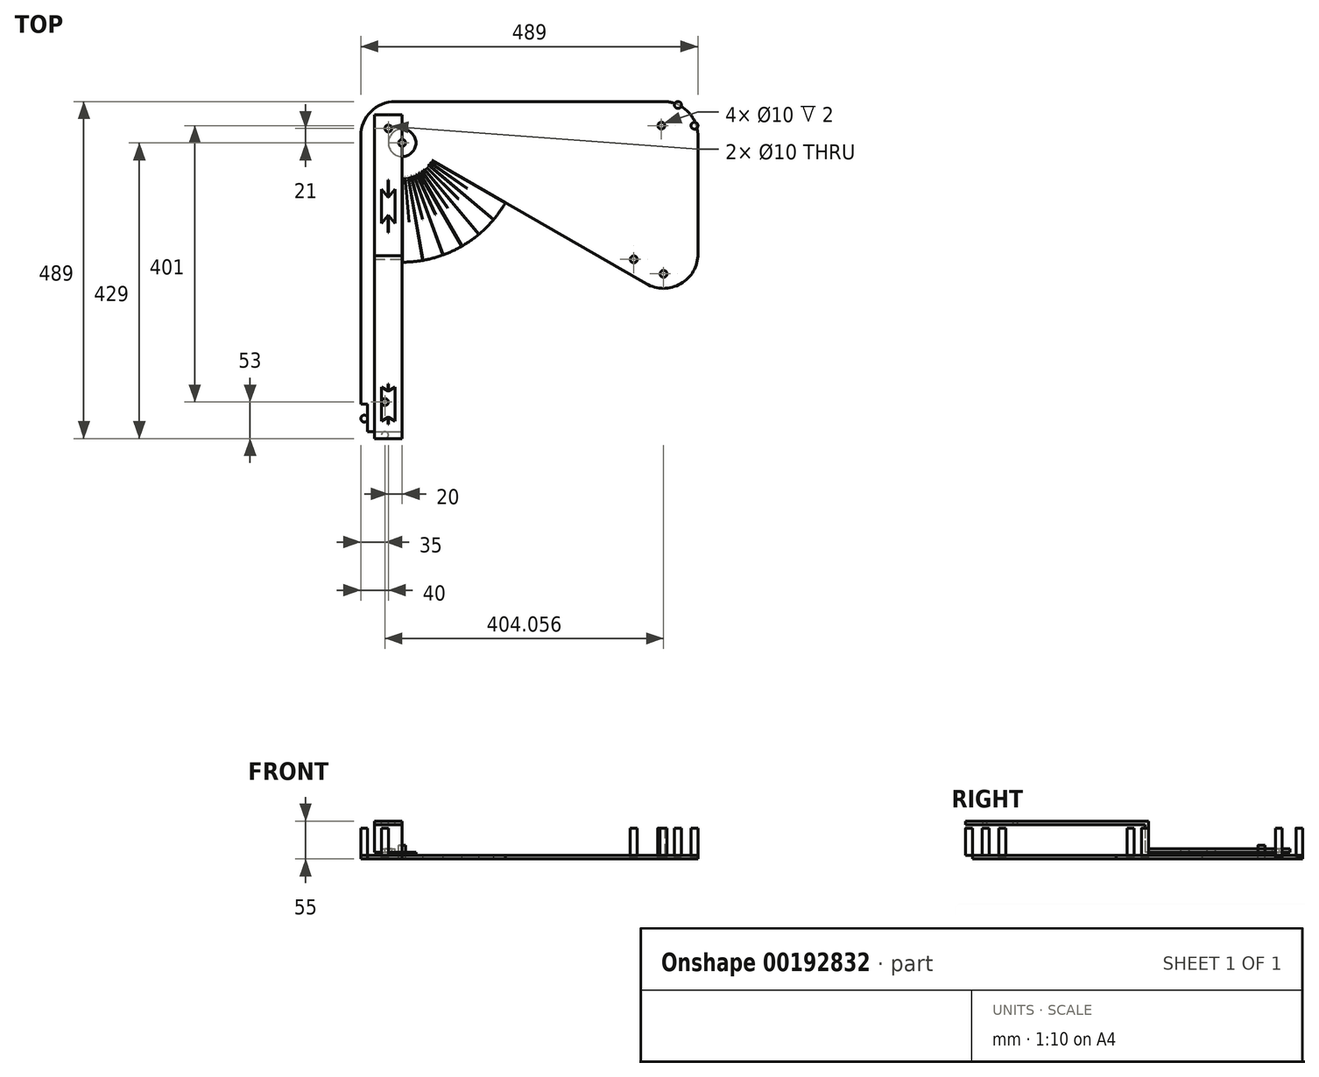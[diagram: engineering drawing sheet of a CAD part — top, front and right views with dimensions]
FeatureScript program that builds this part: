
annotation { "Feature Type Name" : "Feature", "Feature Type Description" : "" }
export const myFeature = defineFeature(function(context is Context, id is Id, definition is map)
    precondition{}
    {
        {
            var Q0;
            Q0=qCreatedBy(makeId("Top.planeOp"),FACE);
            var sketch = newSketch(context, id + "F0", { "sketchPlane" : qUnion([Q0])});
            skLineSegment(sketch, "E0.bottom", {"start": v(0, 0) * mm, "end": v(489, 0) * mm});
            skLineSegment(sketch, "E0.left", {"start": v(0, 0) * mm, "end": v(0, 500) * mm});
            skLineSegment(sketch, "E0.right", {"start": v(489, 0) * mm, "end": v(489, 479) * mm});
            skLineSegment(sketch, "E1.top", {"start": v(0, 0) * mm, "end": v(10, 0) * mm});
            skLineSegment(sketch, "E1.left", {"start": v(0, 489) * mm, "end": v(0, 0) * mm});
            skLineSegment(sketch, "E1.right", {"start": v(10, 50) * mm, "end": v(10, 10) * mm});
            skPoint(sketch, "E2", {"position": v(60, 429) * mm});
            skLineSegment(sketch, "E3", {"start": v(60, 255.9) * mm, "end": v(60, 0) * mm});
            skLineSegment(sketch, "E4", {"start": v(209.9, 342.45) * mm, "end": v(489, 181.32) * mm});
            skLineSegment(sketch, "E5.bottom", {"start": v(10, 48) * mm, "end": v(60, 48) * mm, "construction": true});
            skLineSegment(sketch, "E5.right", {"start": v(60, 48) * mm, "end": v(60, 10) * mm, "construction": true});
            skLineSegment(sketch, "E6.top", {"start": v(441, 429) * mm, "end": v(479, 429) * mm, "construction": true});
            skLineSegment(sketch, "E6.left", {"start": v(441, 479) * mm, "end": v(441, 429) * mm, "construction": true});
            skArc(sketch, "E7", {"start": v(60, 29) * mm, "mid": v(342.84, 146.16) * mm, "end": v(460, 429) * mm, "construction": true});
            skPoint(sketch, "E8", {"position": v(10, 29) * mm});
            skPoint(sketch, "E9", {"position": v(460, 479) * mm});
            skArc(sketch, "E10.0", {"start": v(60, 10) * mm, "mid": v(356.28, 132.72) * mm, "end": v(479, 429) * mm, "construction": true});
            skArc(sketch, "E11.0", {"start": v(60, 48) * mm, "mid": v(329.4, 159.6) * mm, "end": v(441, 429) * mm, "construction": true});
            skLineSegment(sketch, "E12", {"start": v(60, 255.9) * mm, "end": v(209.9, 342.45) * mm, "construction": true});
            skPoint(sketch, "E13.end.orphan", {"position": v(189.9, 354) * mm});
            skPoint(sketch, "E13.start.orphan", {"position": v(60, 279) * mm});
            skCircle(sketch, "E14", {"center": v(60, 429) * mm, "radius": 5 * mm});
            skLineSegment(sketch, "E15.top", {"start": v(489, 489) * mm, "end": v(0, 489) * mm});
            skLineSegment(sketch, "E15.left", {"start": v(489, 479) * mm, "end": v(489, 489) * mm});
            skLineSegment(sketch, "E16", {"start": v(439, 489) * mm, "end": v(439, 479) * mm});
            skLineSegment(sketch, "E17", {"start": v(439, 479) * mm, "end": v(479, 479) * mm});
            skLineSegment(sketch, "E18", {"start": v(479, 479) * mm, "end": v(479, 429) * mm});
            skLineSegment(sketch, "E19", {"start": v(489, 429) * mm, "end": v(479, 429) * mm});
            skArc(sketch, "E20", {"start": v(60, 255.9) * mm, "mid": v(146.55, 279.1) * mm, "end": v(209.9, 342.45) * mm});
            skLineSegment(sketch, "E21", {"start": v(0, 50) * mm, "end": v(10, 50) * mm});
            skLineSegment(sketch, "E22", {"start": v(10, 10) * mm, "end": v(60, 10) * mm});
            skSolve(sketch);
        }
        {
            var Q0;
            {var subQ3=sQuery(id+"F0.wireOp",EDGE,"E1.right");Q0=makeQuery(id+"F0.imprint","IMPRINT",FACE,{"disambiguationData":[TD([[makeQuery(id+"F0.imprint","IMPRINT",EDGE,{"derivedFrom":subQ3}),1.0]])]});}
            var Q1;
            {var subQ2=sQuery(id+"F0.wireOp",EDGE,"E1.top");Q1=makeQuery(id+"F0.imprint","IMPRINT",FACE,{"disambiguationData":[TD([[makeQuery(id+"F0.imprint","IMPRINT",EDGE,{"derivedFrom":subQ2}),1.0]])]});}
            var Q2;
            {var subQ1=sQuery(id+"F0.wireOp",EDGE,"E15.left");Q2=makeQuery(id+"F0.imprint","IMPRINT",FACE,{"disambiguationData":[TD([[makeQuery(id+"F0.imprint","IMPRINT",EDGE,{"derivedFrom":subQ1}),1.0]])]});}
            extrude(context, id + "F1", {"entities" : qUnion([Q0, Q1, Q2]), "depth" : 5 * mm});
        }
        {
            var Q0;
            {var subQ0=sQuery(id+"F0.wireOp",EDGE,"E15.top");Q0=makeQuery(id+"FC8zW7vc6qnoxrJ_1.boolean.opBoolean","MERGE",FACE,{"derivedFrom":[makeQuery(id+"F1.opExtrude","SWEPT_FACE",FACE,{"disambiguationData":[OSD([subQ0])]}),makeQuery(id+"FC8zW7vc6qnoxrJ_1.opExtrude","SWEPT_FACE",FACE,{"disambiguationData":[OSD([subQ0]),TDD([makeQuery(id+"F0.imprint","IMPRINT",EDGE,{"disambiguationData":[TD([[makeQuery(id+"F0.imprint","INTERSECT",VERTEX,{"derivedFrom":[subQ0,sQuery(id+"F0.wireOp",EDGE,"E15.left")]}),-1.0]])],"derivedFrom":subQ0})])]}),makeQuery(id+"FC8zW7vc6qnoxrJ_1.opExtrude","SWEPT_FACE",FACE,{"disambiguationData":[OSD([subQ0]),TDD([makeQuery(id+"F0.imprint","IMPRINT",EDGE,{"disambiguationData":[TD([[makeQuery(id+"F0.imprint","INTERSECT",VERTEX,{"derivedFrom":[sQuery(id+"F0.wireOp",EDGE,"E1.left"),subQ0]}),1.0]])],"derivedFrom":subQ0})])]})]});}
            cPlane(context, id + "F2", {"entities" : qUnion([Q0]), "cplaneType" : CPlaneType.OFFSET, "offset" : 60 * mm, "oppositeDirection" : true, "width" : 150 * mm, "height" : 150 * mm});
        }
        {
            var Q0;
            Q0=qCreatedBy(id+"F2.planeOp",FACE);
            var sketch = newSketch(context, id + "F3", { "sketchPlane" : qUnion([Q0])});
            skLineSegment(sketch, "E23", {"start": v(-60, 20) * mm, "end": v(-60, 0) * mm});
            skLineSegment(sketch, "E24", {"start": v(-60, 20) * mm, "end": v(-65, 20) * mm});
            skLineSegment(sketch, "E25", {"start": v(-65, 20) * mm, "end": v(-65, 10) * mm});
            skLineSegment(sketch, "E26", {"start": v(-65, 10) * mm, "end": v(-80, 10) * mm});
            skLineSegment(sketch, "E27", {"start": v(-80, 10) * mm, "end": v(-80, 5) * mm});
            skLineSegment(sketch, "E28", {"start": v(-80, 5) * mm, "end": v(-65, 5) * mm});
            skLineSegment(sketch, "E29", {"start": v(-65, 5) * mm, "end": v(-65, 0) * mm});
            skLineSegment(sketch, "E30", {"start": v(-65, 0) * mm, "end": v(-60, 0) * mm});
            skSolve(sketch);
        }
        {
            var Q0;
            Q0=qSketchRegion(id+"F3",true);
            var Q1;
            Q1=sQuery(id+"F3.wireOp",EDGE,"E23");
            revolve(context, id + "F4", {"entities" : qUnion([Q0]), "axis" : qUnion([Q1]), "revolveType" : RevolveType.FULL});
        }
        {
            var Q0;
            Q0=makeQuery(id+"F1.opExtrude","CAP_FACE",FACE,{"disambiguationData":[OSD([sQuery(id+"F0.wireOp",EDGE,"E0.bottom"),sQuery(id+"F0.wireOp",EDGE,"E0.top"),sQuery(id+"F0.wireOp",EDGE,"E0.right"),sQuery(id+"F0.wireOp",EDGE,"E1.right"),sQuery(id+"F0.wireOp",EDGE,"E3"),sQuery(id+"F0.wireOp",EDGE,"E4"),sQuery(id+"F0.wireOp",EDGE,"E12"),sQuery(id+"F0.wireOp",EDGE,"E14")])],"isStart":false});
            cPlane(context, id + "F5", {"entities" : qUnion([Q0]), "cplaneType" : CPlaneType.OFFSET, "offset" : 0 * mm, "width" : 150 * mm, "height" : 150 * mm});
        }
        {
            var Q0;
            Q0=qCreatedBy(id+"F5.planeOp",FACE);
            var sketch = newSketch(context, id + "F6", { "sketchPlane" : qUnion([Q0])});
            skCircle(sketch, "E31", {"center": v(35, 53) * mm, "radius": 5 * mm});
            skLineSegment(sketch, "E32.bottom", {"start": v(10, 10) * mm, "end": v(60, 10) * mm, "construction": true});
            skLineSegment(sketch, "E32.top", {"start": v(10, 48) * mm, "end": v(60, 48) * mm, "construction": true});
            skLineSegment(sketch, "E32.left", {"start": v(10, 10) * mm, "end": v(10, 48) * mm, "construction": true});
            skLineSegment(sketch, "E32.right", {"start": v(60, 10) * mm, "end": v(60, 48) * mm, "construction": true});
            skLineSegment(sketch, "E33.bottom", {"start": v(479, 479) * mm, "end": v(441, 479) * mm, "construction": true});
            skLineSegment(sketch, "E33.top", {"start": v(479, 429) * mm, "end": v(441, 429) * mm, "construction": true});
            skLineSegment(sketch, "E33.left", {"start": v(479, 479) * mm, "end": v(479, 429) * mm, "construction": true});
            skLineSegment(sketch, "E33.right", {"start": v(441, 479) * mm, "end": v(441, 429) * mm, "construction": true});
            skArc(sketch, "E34", {"start": v(60, 29) * mm, "mid": v(342.84, 146.16) * mm, "end": v(460, 429) * mm, "construction": true});
            skArc(sketch, "E35.0", {"start": v(60, 10) * mm, "mid": v(356.28, 132.72) * mm, "end": v(479, 429) * mm, "construction": true});
            skArc(sketch, "E36.0", {"start": v(60, 48) * mm, "mid": v(329.4, 159.6) * mm, "end": v(441, 429) * mm, "construction": true});
            skLineSegment(sketch, "E37", {"start": v(460, 429) * mm, "end": v(460, 479) * mm, "construction": true});
            skLineSegment(sketch, "E38", {"start": v(60, 29) * mm, "end": v(10, 29) * mm, "construction": true});
            skCircle(sketch, "E39", {"center": v(436, 454) * mm, "radius": 5 * mm});
            skCircle(sketch, "E40", {"center": v(439.06, 239.02) * mm, "radius": 5 * mm});
            skLineSegment(sketch, "E41", {"start": v(439.06, 239.02) * mm, "end": v(395.9, 260.06) * mm, "construction": true});
            skCircle(sketch, "E42", {"center": v(395.9, 260.06) * mm, "radius": 5 * mm});
            skCircle(sketch, "E43.MirrorC", {"center": v(35, 5) * mm, "radius": 5 * mm});
            skCircle(sketch, "E44", {"center": v(5, 29) * mm, "radius": 5 * mm});
            skLineSegment(sketch, "E45", {"start": v(35, 5) * mm, "end": v(35, 53) * mm, "construction": true});
            skCircle(sketch, "E46.MirrorC", {"center": v(484, 454) * mm, "radius": 5 * mm});
            skLineSegment(sketch, "E47", {"start": v(436, 454) * mm, "end": v(484, 454) * mm, "construction": true});
            skCircle(sketch, "E48", {"center": v(460, 484) * mm, "radius": 5 * mm});
            skLineSegment(sketch, "E49", {"start": v(5, 34) * mm, "end": v(0, 34) * mm});
            skLineSegment(sketch, "E50", {"start": v(0, 34) * mm, "end": v(0, 24) * mm});
            skLineSegment(sketch, "E51", {"start": v(0, 24) * mm, "end": v(5, 24) * mm});
            skLineSegment(sketch, "E52.bottom", {"start": v(30, 5) * mm, "end": v(40, 5) * mm});
            skLineSegment(sketch, "E52.top", {"start": v(30, 0) * mm, "end": v(40, 0) * mm});
            skLineSegment(sketch, "E52.left", {"start": v(30, 5) * mm, "end": v(30, 0) * mm});
            skLineSegment(sketch, "E52.right", {"start": v(40, 5) * mm, "end": v(40, 0) * mm});
            skLineSegment(sketch, "E53.bottom", {"start": v(465, 484) * mm, "end": v(455, 484) * mm});
            skLineSegment(sketch, "E53.top", {"start": v(465, 489) * mm, "end": v(455, 489) * mm});
            skLineSegment(sketch, "E53.left", {"start": v(465, 484) * mm, "end": v(465, 489) * mm});
            skLineSegment(sketch, "E53.right", {"start": v(455, 484) * mm, "end": v(455, 489) * mm});
            skLineSegment(sketch, "E54.bottom", {"start": v(484, 459) * mm, "end": v(489, 459) * mm});
            skLineSegment(sketch, "E54.top", {"start": v(484, 449) * mm, "end": v(489, 449) * mm});
            skLineSegment(sketch, "E54.left", {"start": v(484, 459) * mm, "end": v(484, 449) * mm});
            skLineSegment(sketch, "E54.right", {"start": v(489, 459) * mm, "end": v(489, 449) * mm});
            skSolve(sketch);
        }
        {
            var Q0;
            Q0=makeQuery(id+"F6.imprint","IMPRINT",FACE,{"disambiguationData":[TD([[makeQuery(id+"F6.imprint","IMPRINT",EDGE,{"derivedFrom":sQuery(id+"F6.wireOp",EDGE,"E42")}),1.0]])]});
            var Q1;
            Q1=makeQuery(id+"F6.imprint","IMPRINT",FACE,{"disambiguationData":[TD([[makeQuery(id+"F6.imprint","IMPRINT",EDGE,{"derivedFrom":sQuery(id+"F6.wireOp",EDGE,"E40")}),1.0]])]});
            var Q2;
            Q2=makeQuery(id+"F6.imprint","IMPRINT",FACE,{"disambiguationData":[TD([[makeQuery(id+"F6.imprint","IMPRINT",EDGE,{"derivedFrom":sQuery(id+"F6.wireOp",EDGE,"E39")}),1.0]])]});
            var Q3;
            Q3=makeQuery(id+"F6.imprint","IMPRINT",FACE,{"disambiguationData":[TD([[makeQuery(id+"F6.imprint","IMPRINT",EDGE,{"derivedFrom":sQuery(id+"F6.wireOp",EDGE,"E31")}),1.0]])]});
            var Q4;
            {var subQ0=sQuery(id+"F6.wireOp",EDGE,"E54.left");Q4=makeQuery(id+"F6.imprint","IMPRINT",FACE,{"disambiguationData":[TD([[makeQuery(id+"F6.imprint","IMPRINT",EDGE,{"derivedFrom":subQ0}),-1.0]])]});}
            var Q5;
            {var subQ0=sQuery(id+"F6.wireOp",EDGE,"E54.left");Q5=makeQuery(id+"F6.imprint","IMPRINT",FACE,{"disambiguationData":[TD([[makeQuery(id+"F6.imprint","IMPRINT",EDGE,{"derivedFrom":subQ0}),1.0]])]});}
            var Q6;
            {var subQ0=sQuery(id+"F6.wireOp",EDGE,"E54.bottom");Q6=makeQuery(id+"F6.imprint","IMPRINT",FACE,{"disambiguationData":[TD([[makeQuery(id+"F6.imprint","IMPRINT",EDGE,{"derivedFrom":subQ0}),-1.0]])]});}
            var Q7;
            {var subQ0=sQuery(id+"F6.wireOp",EDGE,"E54.top");Q7=makeQuery(id+"F6.imprint","IMPRINT",FACE,{"disambiguationData":[TD([[makeQuery(id+"F6.imprint","IMPRINT",EDGE,{"derivedFrom":subQ0}),1.0]])]});}
            var Q8;
            {var subQ0=sQuery(id+"F6.wireOp",EDGE,"E53.right");Q8=makeQuery(id+"F6.imprint","IMPRINT",FACE,{"disambiguationData":[TD([[makeQuery(id+"F6.imprint","IMPRINT",EDGE,{"derivedFrom":subQ0}),-1.0]])]});}
            var Q9;
            {var subQ0=sQuery(id+"F6.wireOp",EDGE,"E53.left");Q9=makeQuery(id+"F6.imprint","IMPRINT",FACE,{"disambiguationData":[TD([[makeQuery(id+"F6.imprint","IMPRINT",EDGE,{"derivedFrom":subQ0}),1.0]])]});}
            var Q10;
            {var subQ0=sQuery(id+"F6.wireOp",EDGE,"E53.bottom");Q10=makeQuery(id+"F6.imprint","IMPRINT",FACE,{"disambiguationData":[TD([[makeQuery(id+"F6.imprint","IMPRINT",EDGE,{"derivedFrom":subQ0}),-1.0]])]});}
            var Q11;
            {var subQ0=sQuery(id+"F6.wireOp",EDGE,"E53.bottom");Q11=makeQuery(id+"F6.imprint","IMPRINT",FACE,{"disambiguationData":[TD([[makeQuery(id+"F6.imprint","IMPRINT",EDGE,{"derivedFrom":subQ0}),1.0]])]});}
            var Q12;
            {var subQ0=sQuery(id+"F6.wireOp",EDGE,"E44");var subQ1=makeQuery(id+"F6.imprint","INTERSECT",VERTEX,{"derivedFrom":[subQ0,sQuery(id+"F6.wireOp",EDGE,"E49")]});Q12=makeQuery(id+"F6.imprint","IMPRINT",FACE,{"disambiguationData":[TD([[makeQuery(id+"F6.imprint","IMPRINT",EDGE,{"disambiguationData":[TD([[subQ1,-1.0]])],"derivedFrom":subQ0}),1.0]])]});}
            var Q13;
            {var subQ0=sQuery(id+"F6.wireOp",EDGE,"E52.bottom");Q13=makeQuery(id+"F6.imprint","IMPRINT",FACE,{"disambiguationData":[TD([[makeQuery(id+"F6.imprint","IMPRINT",EDGE,{"derivedFrom":subQ0}),1.0]])]});}
            var Q14;
            {var subQ0=sQuery(id+"F6.wireOp",EDGE,"E52.bottom");Q14=makeQuery(id+"F6.imprint","IMPRINT",FACE,{"disambiguationData":[TD([[makeQuery(id+"F6.imprint","IMPRINT",EDGE,{"derivedFrom":subQ0}),-1.0]])]});}
            var Q15;
            {var subQ0=sQuery(id+"F6.wireOp",EDGE,"E49");Q15=makeQuery(id+"F6.imprint","IMPRINT",FACE,{"disambiguationData":[TD([[makeQuery(id+"F6.imprint","IMPRINT",EDGE,{"derivedFrom":subQ0}),1.0]])]});}
            var Q16;
            {var subQ0=sQuery(id+"F6.wireOp",EDGE,"E51");Q16=makeQuery(id+"F6.imprint","IMPRINT",FACE,{"disambiguationData":[TD([[makeQuery(id+"F6.imprint","IMPRINT",EDGE,{"derivedFrom":subQ0}),1.0]])]});}
            var Q17;
            {var subQ0=sQuery(id+"F6.wireOp",EDGE,"E52.left");Q17=makeQuery(id+"F6.imprint","IMPRINT",FACE,{"disambiguationData":[TD([[makeQuery(id+"F6.imprint","IMPRINT",EDGE,{"derivedFrom":subQ0}),1.0]])]});}
            var Q18;
            {var subQ0=sQuery(id+"F6.wireOp",EDGE,"E52.right");Q18=makeQuery(id+"F6.imprint","IMPRINT",FACE,{"disambiguationData":[TD([[makeQuery(id+"F6.imprint","IMPRINT",EDGE,{"derivedFrom":subQ0}),-1.0]])]});}
            extrude(context, id + "F7", {"entities" : qUnion([Q0, Q1, Q2, Q3, Q4, Q5, Q6, Q7, Q8, Q9, Q10, Q11, Q12, Q13, Q14, Q15, Q16, Q17, Q18]), "operationType" : NewBodyOperationType.REMOVE, "oppositeDirection" : true, "depth" : 2 * mm});
        }
        {
            var Q0;
            {var subQ0=sQuery(id+"F6.wireOp",EDGE,"E44");var subQ1=makeQuery(id+"F6.imprint","INTERSECT",VERTEX,{"derivedFrom":[subQ0,sQuery(id+"F6.wireOp",EDGE,"E49")]});Q0=makeQuery(id+"F6.imprint","IMPRINT",FACE,{"disambiguationData":[TD([[makeQuery(id+"F6.imprint","IMPRINT",EDGE,{"disambiguationData":[TD([[subQ1,-1.0]])],"derivedFrom":subQ0}),1.0]])]});}
            var Q1;
            Q1=makeQuery(id+"F6.imprint","IMPRINT",FACE,{"disambiguationData":[TD([[makeQuery(id+"F6.imprint","IMPRINT",EDGE,{"derivedFrom":sQuery(id+"F6.wireOp",EDGE,"E31")}),1.0]])]});
            var Q2;
            {var subQ0=sQuery(id+"F6.wireOp",EDGE,"E52.bottom");Q2=makeQuery(id+"F6.imprint","IMPRINT",FACE,{"disambiguationData":[TD([[makeQuery(id+"F6.imprint","IMPRINT",EDGE,{"derivedFrom":subQ0}),1.0]])]});}
            var Q3;
            {var subQ0=sQuery(id+"F6.wireOp",EDGE,"E52.bottom");Q3=makeQuery(id+"F6.imprint","IMPRINT",FACE,{"disambiguationData":[TD([[makeQuery(id+"F6.imprint","IMPRINT",EDGE,{"derivedFrom":subQ0}),-1.0]])]});}
            var Q4;
            Q4=makeQuery(id+"F6.imprint","IMPRINT",FACE,{"disambiguationData":[TD([[makeQuery(id+"F6.imprint","IMPRINT",EDGE,{"derivedFrom":sQuery(id+"F6.wireOp",EDGE,"E42")}),1.0]])]});
            var Q5;
            Q5=makeQuery(id+"F6.imprint","IMPRINT",FACE,{"disambiguationData":[TD([[makeQuery(id+"F6.imprint","IMPRINT",EDGE,{"derivedFrom":sQuery(id+"F6.wireOp",EDGE,"E40")}),1.0]])]});
            var Q6;
            {var subQ0=sQuery(id+"F6.wireOp",EDGE,"E53.bottom");Q6=makeQuery(id+"F6.imprint","IMPRINT",FACE,{"disambiguationData":[TD([[makeQuery(id+"F6.imprint","IMPRINT",EDGE,{"derivedFrom":subQ0}),-1.0]])]});}
            var Q7;
            {var subQ0=sQuery(id+"F6.wireOp",EDGE,"E53.bottom");Q7=makeQuery(id+"F6.imprint","IMPRINT",FACE,{"disambiguationData":[TD([[makeQuery(id+"F6.imprint","IMPRINT",EDGE,{"derivedFrom":subQ0}),1.0]])]});}
            var Q8;
            {var subQ0=sQuery(id+"F6.wireOp",EDGE,"E54.left");Q8=makeQuery(id+"F6.imprint","IMPRINT",FACE,{"disambiguationData":[TD([[makeQuery(id+"F6.imprint","IMPRINT",EDGE,{"derivedFrom":subQ0}),-1.0]])]});}
            var Q9;
            {var subQ0=sQuery(id+"F6.wireOp",EDGE,"E54.left");Q9=makeQuery(id+"F6.imprint","IMPRINT",FACE,{"disambiguationData":[TD([[makeQuery(id+"F6.imprint","IMPRINT",EDGE,{"derivedFrom":subQ0}),1.0]])]});}
            var Q10;
            Q10=makeQuery(id+"F6.imprint","IMPRINT",FACE,{"disambiguationData":[TD([[makeQuery(id+"F6.imprint","IMPRINT",EDGE,{"derivedFrom":sQuery(id+"F6.wireOp",EDGE,"E39")}),1.0]])]});
            extrude(context, id + "F8", {"entities" : qUnion([Q0, Q1, Q2, Q3, Q4, Q5, Q6, Q7, Q8, Q9, Q10]), "depth" : 40 * mm});
        }
        {
            var Q0;
            Q0=makeQuery(id+"F1.opExtrude","CAP_FACE",FACE,{"disambiguationData":[OSD([sQuery(id+"F0.wireOp",EDGE,"E0.bottom"),sQuery(id+"F0.wireOp",EDGE,"E0.right"),sQuery(id+"F0.wireOp",EDGE,"E1.right"),sQuery(id+"F0.wireOp",EDGE,"E3"),sQuery(id+"F0.wireOp",EDGE,"E4"),sQuery(id+"F0.wireOp",EDGE,"E12"),sQuery(id+"F0.wireOp",EDGE,"E14"),sQuery(id+"F0.wireOp",EDGE,"E15.top"),sQuery(id+"F0.wireOp",EDGE,"E16"),sQuery(id+"F0.wireOp",EDGE,"E17"),sQuery(id+"F0.wireOp",EDGE,"E18"),sQuery(id+"F0.wireOp",EDGE,"E19")])],"isStart":false});
            var sketch = newSketch(context, id + "F9", { "sketchPlane" : qUnion([Q0])});
            skLineSegment(sketch, "E55", {"start": v(60, 379) * mm, "end": v(60, 255.9) * mm});
            skLineSegment(sketch, "E56", {"start": v(103.3, 404) * mm, "end": v(209.9, 342.45) * mm});
            skArc(sketch, "E57", {"start": v(60, 314) * mm, "mid": v(117.5, 329.4) * mm, "end": v(159.6, 371.5) * mm});
            skLineSegment(sketch, "E58.0", {"start": v(64.45, 426.72) * mm, "end": v(210.03, 342.67) * mm});
            skArc(sketch, "E59", {"start": v(60, 424) * mm, "mid": v(62.6, 424.73) * mm, "end": v(64.45, 426.72) * mm});
            skLineSegment(sketch, "E60.trimOffspring", {"start": v(64.2, 426.29) * mm, "end": v(64.83, 425.92) * mm});
            skLineSegment(sketch, "E61", {"start": v(210.03, 342.67) * mm, "end": v(209.9, 342.45) * mm});
            skLineSegment(sketch, "E62", {"start": v(100.96, 400.32) * mm, "end": v(154.2, 363.04) * mm});
            skLineSegment(sketch, "E63", {"start": v(98.3, 396.86) * mm, "end": v(192.6, 317.74) * mm});
            skLineSegment(sketch, "E64", {"start": v(95.36, 393.64) * mm, "end": v(141.32, 347.68) * mm});
            skLineSegment(sketch, "E65", {"start": v(92.14, 390.7) * mm, "end": v(171.26, 296.4) * mm});
            skLineSegment(sketch, "E66", {"start": v(88.68, 388.04) * mm, "end": v(125.96, 334.8) * mm});
            skLineSegment(sketch, "E67", {"start": v(85, 385.7) * mm, "end": v(146.55, 279.1) * mm});
            skLineSegment(sketch, "E68", {"start": v(81.13, 383.68) * mm, "end": v(108.6, 324.77) * mm});
            skLineSegment(sketch, "E69", {"start": v(77.1, 382.02) * mm, "end": v(119.2, 266.34) * mm});
            skLineSegment(sketch, "E70", {"start": v(72.94, 380.7) * mm, "end": v(89.76, 317.92) * mm});
            skLineSegment(sketch, "E71", {"start": v(68.68, 379.76) * mm, "end": v(90.06, 258.54) * mm});
            skLineSegment(sketch, "E72", {"start": v(64.36, 379.2) * mm, "end": v(70.02, 314.44) * mm});
            skArc(sketch, "E73", {"start": v(60, 255.9) * mm, "mid": v(146.55, 279.1) * mm, "end": v(209.9, 342.45) * mm, "construction": true});
            skPoint(sketch, "E74.orphan", {"position": v(117.5, 329.4) * mm});
            skLineSegment(sketch, "E75.0", {"start": v(64.24, 426.34) * mm, "end": v(64.83, 425.92) * mm});
            skLineSegment(sketch, "E76.0", {"start": v(63.95, 425.93) * mm, "end": v(64.55, 425.51) * mm});
            skLineSegment(sketch, "E77.0", {"start": v(63.67, 425.6) * mm, "end": v(64.23, 425.13) * mm});
            skLineSegment(sketch, "E78.0", {"start": v(64, 425.98) * mm, "end": v(64.55, 425.51) * mm});
            skLineSegment(sketch, "E79.0", {"start": v(63.36, 425.29) * mm, "end": v(63.87, 424.77) * mm});
            skLineSegment(sketch, "E80.0", {"start": v(63.71, 425.64) * mm, "end": v(64.23, 425.13) * mm});
            skLineSegment(sketch, "E81.0", {"start": v(63.02, 425) * mm, "end": v(63.49, 424.45) * mm});
            skLineSegment(sketch, "E82.0", {"start": v(63.4, 425.33) * mm, "end": v(63.87, 424.77) * mm});
            skLineSegment(sketch, "E83.0", {"start": v(63.07, 425.05) * mm, "end": v(63.49, 424.45) * mm});
            skLineSegment(sketch, "E84.0", {"start": v(62.66, 424.76) * mm, "end": v(63.08, 424.17) * mm});
            skLineSegment(sketch, "E85.0", {"start": v(55.7, 435.96) * mm, "end": v(62.65, 423.92) * mm});
            skLineSegment(sketch, "E86.0", {"start": v(56.12, 436.21) * mm, "end": v(63.08, 424.17) * mm});
            skLineSegment(sketch, "E87.0", {"start": v(61.89, 424.36) * mm, "end": v(62.2, 423.7) * mm});
            skLineSegment(sketch, "E88.0", {"start": v(62.34, 424.57) * mm, "end": v(62.65, 423.92) * mm});
            skLineSegment(sketch, "E89.0", {"start": v(61.48, 424.22) * mm, "end": v(61.72, 423.53) * mm});
            skLineSegment(sketch, "E90.0", {"start": v(61.95, 424.39) * mm, "end": v(62.2, 423.7) * mm});
            skLineSegment(sketch, "E91.0", {"start": v(61.05, 424.1) * mm, "end": v(61.24, 423.4) * mm});
            skLineSegment(sketch, "E92.0", {"start": v(61.54, 424.24) * mm, "end": v(61.72, 423.53) * mm});
            skLineSegment(sketch, "E93.0", {"start": v(60.62, 424.03) * mm, "end": v(60.75, 423.32) * mm});
            skLineSegment(sketch, "E94.0", {"start": v(61.11, 424.12) * mm, "end": v(61.24, 423.4) * mm});
            skLineSegment(sketch, "E95.0", {"start": v(60.19, 424) * mm, "end": v(60.25, 423.27) * mm});
            skLineSegment(sketch, "E96.0", {"start": v(60.68, 424.04) * mm, "end": v(60.75, 423.32) * mm});
            skLineSegment(sketch, "E97.0", {"start": v(59.75, 429) * mm, "end": v(59.75, 255.9) * mm});
            skLineSegment(sketch, "E98.0", {"start": v(60.25, 424) * mm, "end": v(60.25, 423.27) * mm});
            skArc(sketch, "E99", {"start": v(103.3, 404) * mm, "mid": v(85, 385.7) * mm, "end": v(60, 379) * mm});
            skLineSegment(sketch, "E100.trimOffspring", {"start": v(60.25, 379) * mm, "end": v(60.25, 255.9) * mm});
            skLineSegment(sketch, "E101.trimOffspring", {"start": v(64.1, 379.17) * mm, "end": v(69.77, 314.42) * mm});
            skLineSegment(sketch, "E102.trimOffspring", {"start": v(64.6, 379.21) * mm, "end": v(70.27, 314.46) * mm});
            skLineSegment(sketch, "E103.trimOffspring", {"start": v(68.44, 379.72) * mm, "end": v(89.81, 258.5) * mm});
            skLineSegment(sketch, "E104.trimOffspring", {"start": v(68.93, 379.8) * mm, "end": v(90.3, 258.58) * mm});
            skLineSegment(sketch, "E105.trimOffspring", {"start": v(72.7, 380.64) * mm, "end": v(89.52, 317.85) * mm});
            skLineSegment(sketch, "E106.trimOffspring", {"start": v(73.18, 380.77) * mm, "end": v(90, 317.98) * mm});
            skLineSegment(sketch, "E107.trimOffspring", {"start": v(76.87, 381.93) * mm, "end": v(118.97, 266.26) * mm});
            skLineSegment(sketch, "E108.trimOffspring", {"start": v(77.34, 382.1) * mm, "end": v(119.44, 266.43) * mm});
            skLineSegment(sketch, "E109.trimOffspring", {"start": v(80.9, 383.58) * mm, "end": v(108.37, 324.67) * mm});
            skLineSegment(sketch, "E110.trimOffspring", {"start": v(81.36, 383.8) * mm, "end": v(108.83, 324.88) * mm});
            skLineSegment(sketch, "E111.trimOffspring", {"start": v(88.47, 387.9) * mm, "end": v(125.76, 334.65) * mm});
            skLineSegment(sketch, "E112.trimOffspring", {"start": v(88.88, 388.19) * mm, "end": v(126.17, 334.94) * mm});
            skLineSegment(sketch, "E113.trimOffspring", {"start": v(84.78, 385.57) * mm, "end": v(146.33, 278.97) * mm});
            skLineSegment(sketch, "E114.trimOffspring", {"start": v(85.22, 385.82) * mm, "end": v(146.76, 279.22) * mm});
            skLineSegment(sketch, "E115.trimOffspring", {"start": v(91.95, 390.54) * mm, "end": v(171.07, 296.24) * mm});
            skLineSegment(sketch, "E116.trimOffspring", {"start": v(92.33, 390.86) * mm, "end": v(171.45, 296.56) * mm});
            skLineSegment(sketch, "E117.trimOffspring", {"start": v(95.18, 393.47) * mm, "end": v(141.14, 347.5) * mm});
            skLineSegment(sketch, "E118.trimOffspring", {"start": v(95.53, 393.82) * mm, "end": v(141.5, 347.86) * mm});
            skLineSegment(sketch, "E119.trimOffspring", {"start": v(98.14, 396.67) * mm, "end": v(192.44, 317.55) * mm});
            skLineSegment(sketch, "E120.trimOffspring", {"start": v(98.46, 397.05) * mm, "end": v(192.76, 317.93) * mm});
            skLineSegment(sketch, "E121.trimOffspring", {"start": v(100.81, 400.12) * mm, "end": v(154.06, 362.83) * mm});
            skLineSegment(sketch, "E122.trimOffspring", {"start": v(101.1, 400.53) * mm, "end": v(154.35, 363.24) * mm});
            skLineSegment(sketch, "E123.trimOffspring", {"start": v(103.18, 403.78) * mm, "end": v(209.78, 342.24) * mm});
            skArc(sketch, "E124", {"start": v(209.9, 342.45) * mm, "mid": v(146.55, 279.1) * mm, "end": v(60, 255.9) * mm});
            skSolve(sketch);
        }
        {
            var Q0;
            {var subQ0=sQuery(id+"F9.wireOp",EDGE,"E99");var subQ1=sQuery(id+"F9.wireOp",EDGE,"E56");var subQ2=makeQuery(id+"F9.imprint","INTERSECT",VERTEX,{"derivedFrom":[subQ1,subQ0]});Q0=makeQuery(id+"F9.imprint","IMPRINT",FACE,{"disambiguationData":[TD([[makeQuery(id+"F9.imprint","IMPRINT",EDGE,{"disambiguationData":[TD([[subQ2,-1.0]])],"derivedFrom":subQ1}),-1.0]])]});}
            var Q1;
            {var subQ0=sQuery(id+"F9.wireOp",EDGE,"E56");var subQ3=sQuery(id+"F9.wireOp",EDGE,"E57");var subQ4=makeQuery(id+"F9.imprint","INTERSECT",VERTEX,{"derivedFrom":[subQ0,subQ3]});Q1=makeQuery(id+"F9.imprint","IMPRINT",FACE,{"disambiguationData":[TD([[makeQuery(id+"F9.imprint","IMPRINT",EDGE,{"disambiguationData":[TD([[subQ4,1.0]])],"derivedFrom":subQ3}),-1.0]])]});}
            var Q2;
            {var subQ0=sQuery(id+"F9.wireOp",EDGE,"E62");Q2=makeQuery(id+"F9.imprint","IMPRINT",FACE,{"disambiguationData":[TD([[makeQuery(id+"F9.imprint","IMPRINT",EDGE,{"derivedFrom":subQ0}),1.0]])]});}
            var Q3;
            {var subQ0=sQuery(id+"F9.wireOp",EDGE,"E62");Q3=makeQuery(id+"F9.imprint","IMPRINT",FACE,{"disambiguationData":[TD([[makeQuery(id+"F9.imprint","IMPRINT",EDGE,{"derivedFrom":subQ0}),-1.0]])]});}
            var Q4;
            {var subQ0=sQuery(id+"F9.wireOp",EDGE,"E63");var subQ1=sQuery(id+"F9.wireOp",EDGE,"E57");var subQ2=makeQuery(id+"F9.imprint","INTERSECT",VERTEX,{"derivedFrom":[subQ1,subQ0]});Q4=makeQuery(id+"F9.imprint","IMPRINT",FACE,{"disambiguationData":[TD([[makeQuery(id+"F9.imprint","IMPRINT",EDGE,{"disambiguationData":[TD([[subQ2,-1.0]])],"derivedFrom":subQ1}),1.0]])]});}
            var Q5;
            {var subQ0=sQuery(id+"F9.wireOp",EDGE,"E119.trimOffspring");var subQ1=sQuery(id+"F9.wireOp",EDGE,"E57");var subQ2=makeQuery(id+"F9.imprint","INTERSECT",VERTEX,{"derivedFrom":[subQ1,subQ0]});Q5=makeQuery(id+"F9.imprint","IMPRINT",FACE,{"disambiguationData":[TD([[makeQuery(id+"F9.imprint","IMPRINT",EDGE,{"disambiguationData":[TD([[subQ2,-1.0]])],"derivedFrom":subQ1}),1.0]])]});}
            var Q6;
            {var subQ0=sQuery(id+"F9.wireOp",EDGE,"E119.trimOffspring");var subQ1=sQuery(id+"F9.wireOp",EDGE,"E57");var subQ2=makeQuery(id+"F9.imprint","INTERSECT",VERTEX,{"derivedFrom":[subQ1,subQ0]});Q6=makeQuery(id+"F9.imprint","IMPRINT",FACE,{"disambiguationData":[TD([[makeQuery(id+"F9.imprint","IMPRINT",EDGE,{"disambiguationData":[TD([[subQ2,-1.0]])],"derivedFrom":subQ1}),-1.0]])]});}
            var Q7;
            {var subQ0=sQuery(id+"F9.wireOp",EDGE,"E63");var subQ1=sQuery(id+"F9.wireOp",EDGE,"E57");var subQ2=makeQuery(id+"F9.imprint","INTERSECT",VERTEX,{"derivedFrom":[subQ1,subQ0]});Q7=makeQuery(id+"F9.imprint","IMPRINT",FACE,{"disambiguationData":[TD([[makeQuery(id+"F9.imprint","IMPRINT",EDGE,{"disambiguationData":[TD([[subQ2,-1.0]])],"derivedFrom":subQ1}),-1.0]])]});}
            var Q8;
            {var subQ0=sQuery(id+"F9.wireOp",EDGE,"E64");Q8=makeQuery(id+"F9.imprint","IMPRINT",FACE,{"disambiguationData":[TD([[makeQuery(id+"F9.imprint","IMPRINT",EDGE,{"derivedFrom":subQ0}),-1.0]])]});}
            var Q9;
            {var subQ0=sQuery(id+"F9.wireOp",EDGE,"E64");Q9=makeQuery(id+"F9.imprint","IMPRINT",FACE,{"disambiguationData":[TD([[makeQuery(id+"F9.imprint","IMPRINT",EDGE,{"derivedFrom":subQ0}),1.0]])]});}
            var Q10;
            {var subQ0=sQuery(id+"F9.wireOp",EDGE,"E65");var subQ1=sQuery(id+"F9.wireOp",EDGE,"E57");var subQ2=makeQuery(id+"F9.imprint","INTERSECT",VERTEX,{"derivedFrom":[subQ1,subQ0]});Q10=makeQuery(id+"F9.imprint","IMPRINT",FACE,{"disambiguationData":[TD([[makeQuery(id+"F9.imprint","IMPRINT",EDGE,{"disambiguationData":[TD([[subQ2,-1.0]])],"derivedFrom":subQ1}),1.0]])]});}
            var Q11;
            {var subQ0=sQuery(id+"F9.wireOp",EDGE,"E65");var subQ1=sQuery(id+"F9.wireOp",EDGE,"E57");var subQ2=makeQuery(id+"F9.imprint","INTERSECT",VERTEX,{"derivedFrom":[subQ1,subQ0]});Q11=makeQuery(id+"F9.imprint","IMPRINT",FACE,{"disambiguationData":[TD([[makeQuery(id+"F9.imprint","IMPRINT",EDGE,{"disambiguationData":[TD([[subQ2,-1.0]])],"derivedFrom":subQ1}),-1.0]])]});}
            var Q12;
            {var subQ0=sQuery(id+"F9.wireOp",EDGE,"E115.trimOffspring");var subQ1=sQuery(id+"F9.wireOp",EDGE,"E57");var subQ2=makeQuery(id+"F9.imprint","INTERSECT",VERTEX,{"derivedFrom":[subQ1,subQ0]});Q12=makeQuery(id+"F9.imprint","IMPRINT",FACE,{"disambiguationData":[TD([[makeQuery(id+"F9.imprint","IMPRINT",EDGE,{"disambiguationData":[TD([[subQ2,-1.0]])],"derivedFrom":subQ1}),-1.0]])]});}
            var Q13;
            {var subQ0=sQuery(id+"F9.wireOp",EDGE,"E115.trimOffspring");var subQ1=sQuery(id+"F9.wireOp",EDGE,"E57");var subQ2=makeQuery(id+"F9.imprint","INTERSECT",VERTEX,{"derivedFrom":[subQ1,subQ0]});Q13=makeQuery(id+"F9.imprint","IMPRINT",FACE,{"disambiguationData":[TD([[makeQuery(id+"F9.imprint","IMPRINT",EDGE,{"disambiguationData":[TD([[subQ2,-1.0]])],"derivedFrom":subQ1}),1.0]])]});}
            var Q14;
            {var subQ0=sQuery(id+"F9.wireOp",EDGE,"E66");Q14=makeQuery(id+"F9.imprint","IMPRINT",FACE,{"disambiguationData":[TD([[makeQuery(id+"F9.imprint","IMPRINT",EDGE,{"derivedFrom":subQ0}),1.0]])]});}
            var Q15;
            {var subQ0=sQuery(id+"F9.wireOp",EDGE,"E66");Q15=makeQuery(id+"F9.imprint","IMPRINT",FACE,{"disambiguationData":[TD([[makeQuery(id+"F9.imprint","IMPRINT",EDGE,{"derivedFrom":subQ0}),-1.0]])]});}
            var Q16;
            {var subQ0=sQuery(id+"F9.wireOp",EDGE,"E114.trimOffspring");var subQ1=sQuery(id+"F9.wireOp",EDGE,"E57");var subQ2=makeQuery(id+"F9.imprint","INTERSECT",VERTEX,{"derivedFrom":[subQ1,subQ0]});Q16=makeQuery(id+"F9.imprint","IMPRINT",FACE,{"disambiguationData":[TD([[makeQuery(id+"F9.imprint","IMPRINT",EDGE,{"disambiguationData":[TD([[subQ2,1.0]])],"derivedFrom":subQ1}),1.0]])]});}
            var Q17;
            {var subQ0=sQuery(id+"F9.wireOp",EDGE,"E113.trimOffspring");var subQ1=sQuery(id+"F9.wireOp",EDGE,"E57");var subQ2=makeQuery(id+"F9.imprint","INTERSECT",VERTEX,{"derivedFrom":[subQ1,subQ0]});Q17=makeQuery(id+"F9.imprint","IMPRINT",FACE,{"disambiguationData":[TD([[makeQuery(id+"F9.imprint","IMPRINT",EDGE,{"disambiguationData":[TD([[subQ2,-1.0]])],"derivedFrom":subQ1}),1.0]])]});}
            var Q18;
            {var subQ0=sQuery(id+"F9.wireOp",EDGE,"E68");Q18=makeQuery(id+"F9.imprint","IMPRINT",FACE,{"disambiguationData":[TD([[makeQuery(id+"F9.imprint","IMPRINT",EDGE,{"derivedFrom":subQ0}),-1.0]])]});}
            var Q19;
            {var subQ0=sQuery(id+"F9.wireOp",EDGE,"E68");Q19=makeQuery(id+"F9.imprint","IMPRINT",FACE,{"disambiguationData":[TD([[makeQuery(id+"F9.imprint","IMPRINT",EDGE,{"derivedFrom":subQ0}),1.0]])]});}
            var Q20;
            {var subQ0=sQuery(id+"F9.wireOp",EDGE,"E69");var subQ1=sQuery(id+"F9.wireOp",EDGE,"E57");var subQ2=makeQuery(id+"F9.imprint","INTERSECT",VERTEX,{"derivedFrom":[subQ1,subQ0]});Q20=makeQuery(id+"F9.imprint","IMPRINT",FACE,{"disambiguationData":[TD([[makeQuery(id+"F9.imprint","IMPRINT",EDGE,{"disambiguationData":[TD([[subQ2,-1.0]])],"derivedFrom":subQ1}),1.0]])]});}
            var Q21;
            {var subQ0=sQuery(id+"F9.wireOp",EDGE,"E107.trimOffspring");var subQ1=sQuery(id+"F9.wireOp",EDGE,"E57");var subQ2=makeQuery(id+"F9.imprint","INTERSECT",VERTEX,{"derivedFrom":[subQ1,subQ0]});Q21=makeQuery(id+"F9.imprint","IMPRINT",FACE,{"disambiguationData":[TD([[makeQuery(id+"F9.imprint","IMPRINT",EDGE,{"disambiguationData":[TD([[subQ2,-1.0]])],"derivedFrom":subQ1}),1.0]])]});}
            var Q22;
            {var subQ0=sQuery(id+"F9.wireOp",EDGE,"E107.trimOffspring");var subQ1=sQuery(id+"F9.wireOp",EDGE,"E57");var subQ2=makeQuery(id+"F9.imprint","INTERSECT",VERTEX,{"derivedFrom":[subQ1,subQ0]});Q22=makeQuery(id+"F9.imprint","IMPRINT",FACE,{"disambiguationData":[TD([[makeQuery(id+"F9.imprint","IMPRINT",EDGE,{"disambiguationData":[TD([[subQ2,-1.0]])],"derivedFrom":subQ1}),-1.0]])]});}
            var Q23;
            {var subQ0=sQuery(id+"F9.wireOp",EDGE,"E69");var subQ1=sQuery(id+"F9.wireOp",EDGE,"E57");var subQ2=makeQuery(id+"F9.imprint","INTERSECT",VERTEX,{"derivedFrom":[subQ1,subQ0]});Q23=makeQuery(id+"F9.imprint","IMPRINT",FACE,{"disambiguationData":[TD([[makeQuery(id+"F9.imprint","IMPRINT",EDGE,{"disambiguationData":[TD([[subQ2,-1.0]])],"derivedFrom":subQ1}),-1.0]])]});}
            var Q24;
            {var subQ0=sQuery(id+"F9.wireOp",EDGE,"E70");Q24=makeQuery(id+"F9.imprint","IMPRINT",FACE,{"disambiguationData":[TD([[makeQuery(id+"F9.imprint","IMPRINT",EDGE,{"derivedFrom":subQ0}),1.0]])]});}
            var Q25;
            {var subQ0=sQuery(id+"F9.wireOp",EDGE,"E70");Q25=makeQuery(id+"F9.imprint","IMPRINT",FACE,{"disambiguationData":[TD([[makeQuery(id+"F9.imprint","IMPRINT",EDGE,{"derivedFrom":subQ0}),-1.0]])]});}
            var Q26;
            {var subQ0=sQuery(id+"F9.wireOp",EDGE,"E71");var subQ1=sQuery(id+"F9.wireOp",EDGE,"E57");var subQ2=makeQuery(id+"F9.imprint","INTERSECT",VERTEX,{"derivedFrom":[subQ1,subQ0]});Q26=makeQuery(id+"F9.imprint","IMPRINT",FACE,{"disambiguationData":[TD([[makeQuery(id+"F9.imprint","IMPRINT",EDGE,{"disambiguationData":[TD([[subQ2,-1.0]])],"derivedFrom":subQ1}),1.0]])]});}
            var Q27;
            {var subQ0=sQuery(id+"F9.wireOp",EDGE,"E103.trimOffspring");var subQ1=sQuery(id+"F9.wireOp",EDGE,"E57");var subQ2=makeQuery(id+"F9.imprint","INTERSECT",VERTEX,{"derivedFrom":[subQ1,subQ0]});Q27=makeQuery(id+"F9.imprint","IMPRINT",FACE,{"disambiguationData":[TD([[makeQuery(id+"F9.imprint","IMPRINT",EDGE,{"disambiguationData":[TD([[subQ2,-1.0]])],"derivedFrom":subQ1}),1.0]])]});}
            var Q28;
            {var subQ0=sQuery(id+"F9.wireOp",EDGE,"E103.trimOffspring");var subQ1=sQuery(id+"F9.wireOp",EDGE,"E57");var subQ2=makeQuery(id+"F9.imprint","INTERSECT",VERTEX,{"derivedFrom":[subQ1,subQ0]});Q28=makeQuery(id+"F9.imprint","IMPRINT",FACE,{"disambiguationData":[TD([[makeQuery(id+"F9.imprint","IMPRINT",EDGE,{"disambiguationData":[TD([[subQ2,-1.0]])],"derivedFrom":subQ1}),-1.0]])]});}
            var Q29;
            {var subQ0=sQuery(id+"F9.wireOp",EDGE,"E71");var subQ1=sQuery(id+"F9.wireOp",EDGE,"E57");var subQ2=makeQuery(id+"F9.imprint","INTERSECT",VERTEX,{"derivedFrom":[subQ1,subQ0]});Q29=makeQuery(id+"F9.imprint","IMPRINT",FACE,{"disambiguationData":[TD([[makeQuery(id+"F9.imprint","IMPRINT",EDGE,{"disambiguationData":[TD([[subQ2,-1.0]])],"derivedFrom":subQ1}),-1.0]])]});}
            var Q30;
            {var subQ0=sQuery(id+"F9.wireOp",EDGE,"E72");Q30=makeQuery(id+"F9.imprint","IMPRINT",FACE,{"disambiguationData":[TD([[makeQuery(id+"F9.imprint","IMPRINT",EDGE,{"derivedFrom":subQ0}),1.0]])]});}
            var Q31;
            {var subQ0=sQuery(id+"F9.wireOp",EDGE,"E72");Q31=makeQuery(id+"F9.imprint","IMPRINT",FACE,{"disambiguationData":[TD([[makeQuery(id+"F9.imprint","IMPRINT",EDGE,{"derivedFrom":subQ0}),-1.0]])]});}
            var Q32;
            {var subQ6=sQuery(id+"F9.wireOp",EDGE,"E55");Q32=makeQuery(id+"F9.imprint","IMPRINT",FACE,{"disambiguationData":[TD([[makeQuery(id+"F9.imprint","IMPRINT",EDGE,{"derivedFrom":subQ6}),1.0]])]});}
            var Q33;
            {var subQ0=sQuery(id+"F9.wireOp",EDGE,"E113.trimOffspring");var subQ1=sQuery(id+"F9.wireOp",EDGE,"E57");var subQ2=makeQuery(id+"F9.imprint","INTERSECT",VERTEX,{"derivedFrom":[subQ1,subQ0]});Q33=makeQuery(id+"F9.imprint","IMPRINT",FACE,{"disambiguationData":[TD([[makeQuery(id+"F9.imprint","IMPRINT",EDGE,{"disambiguationData":[TD([[subQ2,-1.0]])],"derivedFrom":subQ1}),-1.0]])]});}
            var Q34;
            {var subQ0=sQuery(id+"F9.wireOp",EDGE,"E67");var subQ1=sQuery(id+"F9.wireOp",EDGE,"E57");var subQ2=makeQuery(id+"F9.imprint","INTERSECT",VERTEX,{"derivedFrom":[subQ1,subQ0]});Q34=makeQuery(id+"F9.imprint","IMPRINT",FACE,{"disambiguationData":[TD([[makeQuery(id+"F9.imprint","IMPRINT",EDGE,{"disambiguationData":[TD([[subQ2,-1.0]])],"derivedFrom":subQ1}),-1.0]])]});}
            extrude(context, id + "F10", {"entities" : qUnion([Q0, Q1, Q2, Q3, Q4, Q5, Q6, Q7, Q8, Q9, Q10, Q11, Q12, Q13, Q14, Q15, Q16, Q17, Q18, Q19, Q20, Q21, Q22, Q23, Q24, Q25, Q26, Q27, Q28, Q29, Q30, Q31, Q32, Q33, Q34]), "operationType" : NewBodyOperationType.REMOVE, "oppositeDirection" : true, "depth" : 0.5 * mm});
        }
        {
            var Q0;
            Q0=makeQuery(id+"F10.boolean.opBoolean","MERGE",FACE,{"derivedFrom":[makeQuery(id+"F1.opExtrude","SWEPT_FACE",FACE,{"disambiguationData":[OSD([sQuery(id+"F0.wireOp",EDGE,"E3")])]}),makeQuery(id+"F10.opExtrude","SWEPT_FACE",FACE,{"disambiguationData":[OSD([sQuery(id+"F9.wireOp",EDGE,"E55")])]})]});
            var sketch = newSketch(context, id + "F11", { "sketchPlane" : qUnion([Q0])});
            skLineSegment(sketch, "E125.bottom", {"start": v(470, 10) * mm, "end": v(260, 10) * mm});
            skLineSegment(sketch, "E125.top", {"start": v(470, 15) * mm, "end": v(265, 15) * mm});
            skLineSegment(sketch, "E125.left", {"start": v(470, 10) * mm, "end": v(470, 15) * mm});
            skLineSegment(sketch, "E126", {"start": v(265, 15) * mm, "end": v(265, 55) * mm});
            skLineSegment(sketch, "E127", {"start": v(265, 55) * mm, "end": v(0, 55) * mm});
            skLineSegment(sketch, "E128", {"start": v(0, 55) * mm, "end": v(0, 50) * mm});
            skLineSegment(sketch, "E129", {"start": v(0, 50) * mm, "end": v(260, 50) * mm});
            skLineSegment(sketch, "E130", {"start": v(260, 50) * mm, "end": v(260, 10) * mm});
            skPoint(sketch, "E131.trimOffspring.end.orphan", {"position": v(0, 35) * mm});
            skSolve(sketch);
        }
        {
            var Q0;
            Q0=qSketchRegion(id+"F11",true);
            extrude(context, id + "F12", {"entities" : qUnion([Q0]), "oppositeDirection" : true, "depth" : 40 * mm});
        }
        {
            var Q0;
            Q0=makeQuery(id+"F12.opExtrude","SWEPT_FACE",FACE,{"disambiguationData":[OSD([sQuery(id+"F11.wireOp",EDGE,"E125.top")])]});
            var sketch = newSketch(context, id + "F13", { "sketchPlane" : qUnion([Q0])});
            skCircle(sketch, "E132", {"center": v(40, 450) * mm, "radius": 5 * mm});
            skPoint(sketch, "E132.centerSnap0", {"position": v(40, 470) * mm});
            skSolve(sketch);
        }
        {
            var Q0;
            Q0=qSketchRegion(id+"F13",true);
            extrude(context, id + "F14", {"entities" : qUnion([Q0]), "operationType" : NewBodyOperationType.REMOVE, "oppositeDirection" : true, "depth" : 10 * mm});
        }
        {
            var Q0;
            Q0=makeQuery(id+"F12.opExtrude","SWEPT_FACE",FACE,{"disambiguationData":[OSD([sQuery(id+"F11.wireOp",EDGE,"E125.top")])]});
            var sketch = newSketch(context, id + "F15", { "sketchPlane" : qUnion([Q0])});
            skLineSegment(sketch, "E133.bottom", {"start": v(30, 362.1) * mm, "end": v(50, 362.1) * mm});
            skLineSegment(sketch, "E133.top", {"start": v(30, 312.1) * mm, "end": v(50, 312.1) * mm});
            skLineSegment(sketch, "E133.left", {"start": v(30, 362.1) * mm, "end": v(30, 312.1) * mm});
            skLineSegment(sketch, "E133.right", {"start": v(50, 362.1) * mm, "end": v(50, 312.1) * mm});
            skPoint(sketch, "E133.middle", {"position": v(40, 337.1) * mm});
            skPoint(sketch, "E133.middle.positionSnap0", {"position": v(40, 470) * mm});
            skPoint(sketch, "E133.centerSnap0", {"position": v(40, 470) * mm});
            skLineSegment(sketch, "E134", {"start": v(30, 362.1) * mm, "end": v(40, 350.1) * mm});
            skLineSegment(sketch, "E135", {"start": v(40, 350.1) * mm, "end": v(50, 362.1) * mm});
            skLineSegment(sketch, "E136", {"start": v(30, 312.1) * mm, "end": v(40, 324.1) * mm});
            skPoint(sketch, "E136.endSnap0", {"position": v(40, 312.1) * mm});
            skLineSegment(sketch, "E137", {"start": v(40, 324.1) * mm, "end": v(50, 312.1) * mm});
            skSolve(sketch);
        }
        {
            var Q0;
            Q0=makeQuery(id+"F15.imprint","IMPRINT",FACE,{"disambiguationData":[TD([[makeQuery(id+"F15.imprint","IMPRINT",EDGE,{"derivedFrom":sQuery(id+"F15.wireOp",EDGE,"E133.left")}),1.0]])]});
            extrude(context, id + "F16", {"entities" : qUnion([Q0]), "operationType" : NewBodyOperationType.REMOVE, "oppositeDirection" : true, "depth" : 10 * mm});
        }
        {
            var Q0;
            Q0=makeQuery(id+"F12.opExtrude","SWEPT_FACE",FACE,{"disambiguationData":[OSD([sQuery(id+"F11.wireOp",EDGE,"E127")])]});
            var sketch = newSketch(context, id + "F17", { "sketchPlane" : qUnion([Q0])});
            skLineSegment(sketch, "E138.bottom", {"start": v(30, 75) * mm, "end": v(50, 75) * mm});
            skLineSegment(sketch, "E138.top", {"start": v(30, 25) * mm, "end": v(50, 25) * mm});
            skLineSegment(sketch, "E138.left", {"start": v(30, 75) * mm, "end": v(30, 25) * mm});
            skLineSegment(sketch, "E138.right", {"start": v(50, 75) * mm, "end": v(50, 25) * mm});
            skPoint(sketch, "E138.middle", {"position": v(40, 50) * mm});
            skPoint(sketch, "E138.middle.positionSnap0", {"position": v(40, 0) * mm});
            skPoint(sketch, "E138.centerSnap0", {"position": v(40, 0) * mm});
            skLineSegment(sketch, "E139", {"start": v(30, 75) * mm, "end": v(40, 69) * mm});
            skPoint(sketch, "E139.endSnap0", {"position": v(40, 25) * mm});
            skLineSegment(sketch, "E140", {"start": v(40, 69) * mm, "end": v(50, 75) * mm});
            skLineSegment(sketch, "E141", {"start": v(30, 25) * mm, "end": v(40, 31) * mm});
            skLineSegment(sketch, "E142", {"start": v(40, 31) * mm, "end": v(50, 25) * mm});
            skSolve(sketch);
        }
        {
            var Q0;
            Q0=makeQuery(id+"F17.imprint","IMPRINT",FACE,{"disambiguationData":[TD([[makeQuery(id+"F17.imprint","IMPRINT",EDGE,{"derivedFrom":sQuery(id+"F17.wireOp",EDGE,"E138.left")}),1.0]])]});
            extrude(context, id + "F18", {"entities" : qUnion([Q0]), "operationType" : NewBodyOperationType.REMOVE, "oppositeDirection" : true, "depth" : 10 * mm});
        }
        {
            var Q0;
            Q0=makeQuery(id+"F12.opExtrude","SWEPT_FACE",FACE,{"disambiguationData":[OSD([sQuery(id+"F11.wireOp",EDGE,"E125.top")])]});
            var sketch = newSketch(context, id + "F19", { "sketchPlane" : qUnion([Q0])});
            skLineSegment(sketch, "E143", {"start": v(40, 350.1) * mm, "end": v(40, 375.1) * mm});
            skLineSegment(sketch, "E144", {"start": v(40, 375.1) * mm, "end": v(40.25, 375.1) * mm});
            skLineSegment(sketch, "E145", {"start": v(40.25, 375.1) * mm, "end": v(40.25, 350.4) * mm});
            skLineSegment(sketch, "E146", {"start": v(40, 375.1) * mm, "end": v(39.75, 375.1) * mm});
            skLineSegment(sketch, "E147", {"start": v(39.75, 375.1) * mm, "end": v(39.75, 350.4) * mm});
            skLineSegment(sketch, "E148", {"start": v(39.75, 350.4) * mm, "end": v(40, 350.1) * mm});
            skLineSegment(sketch, "E149", {"start": v(40.25, 350.4) * mm, "end": v(40, 350.1) * mm});
            skLineSegment(sketch, "E150", {"start": v(40, 324.1) * mm, "end": v(40, 299.1) * mm});
            skLineSegment(sketch, "E151", {"start": v(40, 299.1) * mm, "end": v(40.25, 299.1) * mm});
            skLineSegment(sketch, "E152", {"start": v(40.25, 299.1) * mm, "end": v(40.25, 323.8) * mm});
            skLineSegment(sketch, "E153", {"start": v(40.25, 323.8) * mm, "end": v(40, 324.1) * mm});
            skLineSegment(sketch, "E154", {"start": v(40, 299.1) * mm, "end": v(39.75, 299.1) * mm});
            skLineSegment(sketch, "E155", {"start": v(39.75, 299.1) * mm, "end": v(39.75, 323.8) * mm});
            skLineSegment(sketch, "E156", {"start": v(39.75, 323.8) * mm, "end": v(40, 324.1) * mm});
            skSolve(sketch);
        }
        {
            var Q0;
            Q0=qSketchRegion(id+"F19",true);
            extrude(context, id + "F20", {"entities" : qUnion([Q0]), "operationType" : NewBodyOperationType.REMOVE, "oppositeDirection" : true, "depth" : 0.5 * mm});
        }
        {
            var Q0;
            Q0=makeQuery(id+"F12.opExtrude","SWEPT_FACE",FACE,{"disambiguationData":[OSD([sQuery(id+"F11.wireOp",EDGE,"E127")])]});
            var sketch = newSketch(context, id + "F21", { "sketchPlane" : qUnion([Q0])});
            skLineSegment(sketch, "E157", {"start": v(40, 69) * mm, "end": v(40, 79) * mm});
            skLineSegment(sketch, "E158", {"start": v(40, 79) * mm, "end": v(40.25, 79) * mm});
            skLineSegment(sketch, "E159", {"start": v(40.25, 79) * mm, "end": v(40.25, 69.15) * mm});
            skLineSegment(sketch, "E160", {"start": v(40.25, 69.15) * mm, "end": v(40, 69) * mm});
            skLineSegment(sketch, "E161", {"start": v(40, 79) * mm, "end": v(39.75, 79) * mm});
            skLineSegment(sketch, "E162", {"start": v(39.75, 79) * mm, "end": v(39.75, 69.15) * mm});
            skLineSegment(sketch, "E163", {"start": v(39.75, 69.15) * mm, "end": v(40, 69) * mm});
            skLineSegment(sketch, "E164", {"start": v(40, 31) * mm, "end": v(40, 21) * mm});
            skLineSegment(sketch, "E165", {"start": v(40, 21) * mm, "end": v(40.25, 21) * mm});
            skLineSegment(sketch, "E166", {"start": v(40.25, 21) * mm, "end": v(40.25, 30.85) * mm});
            skLineSegment(sketch, "E167", {"start": v(40.25, 30.85) * mm, "end": v(40, 31) * mm});
            skLineSegment(sketch, "E168", {"start": v(40, 21) * mm, "end": v(39.75, 21) * mm});
            skLineSegment(sketch, "E169", {"start": v(39.75, 21) * mm, "end": v(39.75, 30.85) * mm});
            skLineSegment(sketch, "E170", {"start": v(39.75, 30.85) * mm, "end": v(40, 31) * mm});
            skSolve(sketch);
        }
        {
            var Q0;
            Q0=qSketchRegion(id+"F21",true);
            extrude(context, id + "F22", {"entities" : qUnion([Q0]), "operationType" : NewBodyOperationType.REMOVE, "oppositeDirection" : true, "depth" : 0.25 * mm});
        }
        {
            var Q0;
            Q0=makeQuery(id+"F1.opExtrude","SWEPT_EDGE",EDGE,{"disambiguationData":[OSD([sQuery(id+"F0.wireOp",EDGE,"E1.left"),sQuery(id+"F0.wireOp",EDGE,"E15.top")])]});
            var Q1;
            Q1=makeQuery(id+"F1.opExtrude","SWEPT_EDGE",EDGE,{"disambiguationData":[OSD([sQuery(id+"F0.wireOp",EDGE,"E0.right"),sQuery(id+"F0.wireOp",EDGE,"E4")])]});
            fillet(context, id + "F23", {"entities" : qUnion([Q0, Q1]), "radius" : 50 * mm, "tangentPropagation" : true, "allowEdgeOverflow" : false});
        }
    });
